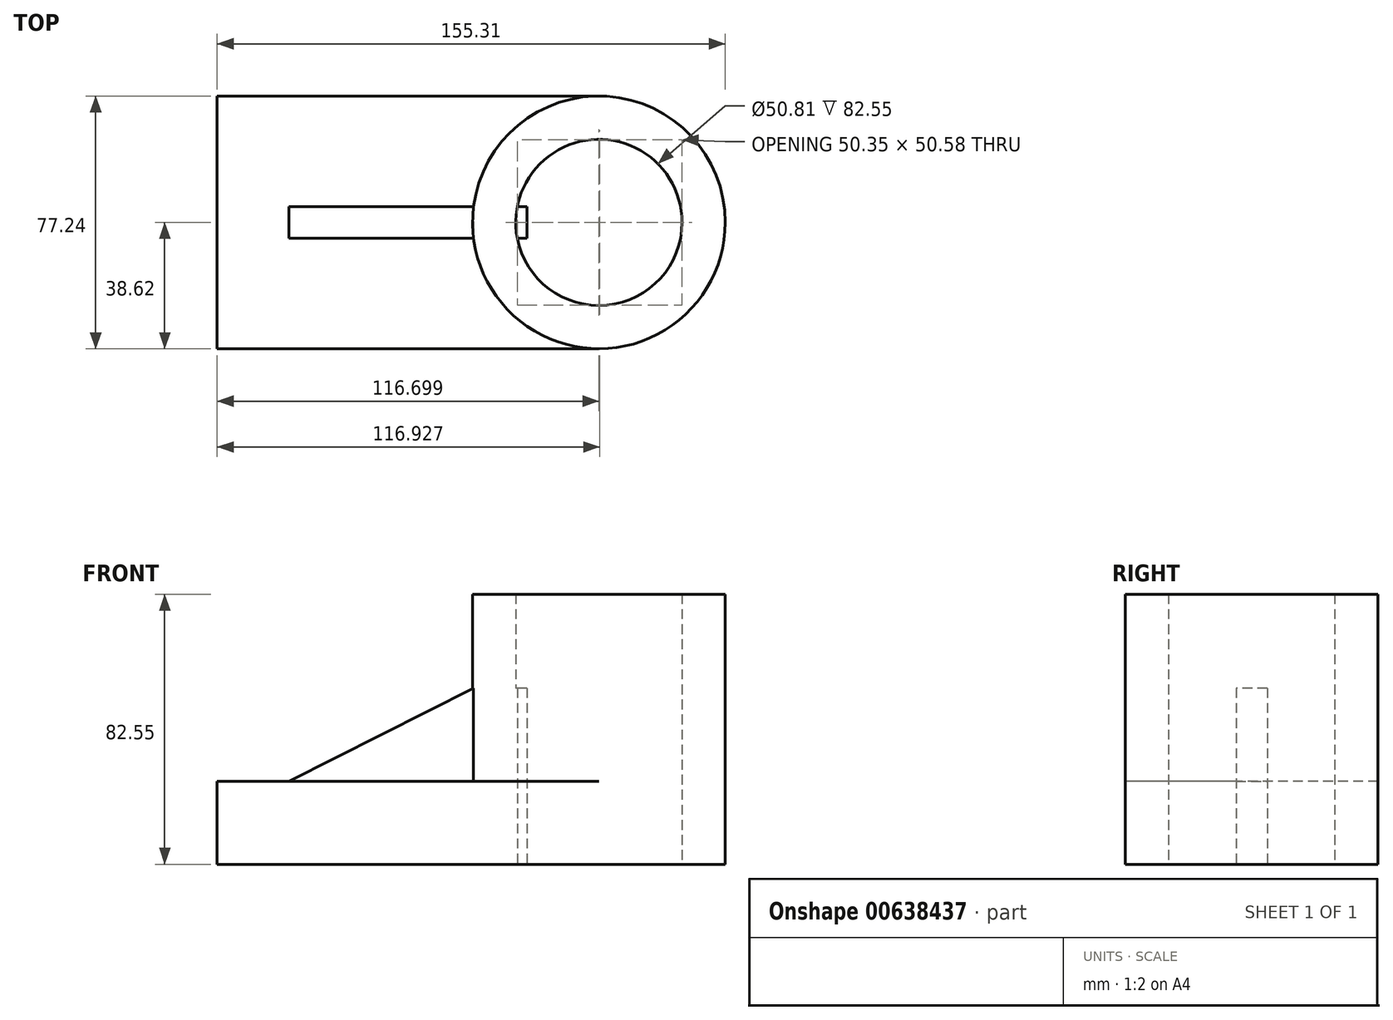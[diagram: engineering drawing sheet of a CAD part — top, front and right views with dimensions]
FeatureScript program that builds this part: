
annotation { "Feature Type Name" : "Feature", "Feature Type Description" : "" }
export const myFeature = defineFeature(function(context is Context, id is Id, definition is map)
    precondition{}
    {
        {
            var Q0;
            Q0=qCreatedBy(makeId("Top.planeOp"),FACE);
            var sketch = newSketch(context, id + "F0", { "sketchPlane" : qUnion([Q0])});
            skLineSegment(sketch, "E0.bottom", {"start": v(-58.35, 38.62) * mm, "end": v(58.35, 38.62) * mm});
            skLineSegment(sketch, "E0.top", {"start": v(-58.35, -38.62) * mm, "end": v(58.35, -38.62) * mm});
            skLineSegment(sketch, "E0.left", {"start": v(-58.35, 38.62) * mm, "end": v(-58.35, -38.62) * mm});
            skPoint(sketch, "E0.middle", {"position": v(0, 0) * mm});
            skCircle(sketch, "E1", {"center": v(58.35, 0) * mm, "radius": 38.62 * mm});
            skCircle(sketch, "E2", {"center": v(58.35, 0) * mm, "radius": 25.4 * mm});
            skSolve(sketch);
        }
        {
            var Q0;
            Q0=makeQuery(id+"F0.imprint","IMPRINT",FACE,{"disambiguationData":[TD([[makeQuery(id+"F0.imprint","IMPRINT",EDGE,{"derivedFrom":sQuery(id+"F0.wireOp",EDGE,"E2")}),-1.0]])]});
            extrude(context, id + "F1", {"entities" : qUnion([Q0]), "depth" : 82.55 * mm, "offsetDistance" : 25.4 * mm});
        }
        {
            var Q0;
            {var subQ0=sQuery(id+"F0.wireOp",EDGE,"E0.bottom");Q0=makeQuery(id+"F0.imprint","IMPRINT",FACE,{"disambiguationData":[TD([[makeQuery(id+"F0.imprint","IMPRINT",EDGE,{"derivedFrom":subQ0}),-1.0]])]});}
            extrude(context, id + "F2", {"entities" : qUnion([Q0]), "operationType" : NewBodyOperationType.ADD, "depth" : 25.4 * mm, "offsetDistance" : 25.4 * mm});
        }
        {
            var Q0;
            Q0=qCreatedBy(makeId("Top.planeOp"),FACE);
            var sketch = newSketch(context, id + "F3", { "sketchPlane" : qUnion([Q0])});
            skLineSegment(sketch, "E3.bottom", {"start": v(36.4, 4.8) * mm, "end": v(-36.4, 4.8) * mm});
            skLineSegment(sketch, "E3.top", {"start": v(36.4, -4.8) * mm, "end": v(-36.4, -4.8) * mm});
            skLineSegment(sketch, "E3.left", {"start": v(36.4, 4.8) * mm, "end": v(36.4, -4.8) * mm});
            skLineSegment(sketch, "E3.right", {"start": v(-36.4, 4.8) * mm, "end": v(-36.4, -4.8) * mm});
            skPoint(sketch, "E3.middle", {"position": v(0, 0) * mm});
            skSolve(sketch);
        }
        {
            var Q0;
            Q0 = qSketchRegion(id + "F3", true);
            extrude(context, id + "F4", {"entities" : qUnion([Q0]), "operationType" : NewBodyOperationType.ADD, "depth" : 53.85 * mm, "offsetDistance" : 25.4 * mm});
        }
        {
            var Q0;
            {var subQ2=sQuery(id+"F3.wireOp",EDGE,"E3.top");var subQ4=sQuery(id+"F0.wireOp",EDGE,"E1");Q0=makeQuery(id+"F4.boolean.opBoolean","SPLIT",FACE,{"disambiguationData":[TD([makeQuery(id+"F1.opExtrude","SWEPT_FACE",FACE,{"disambiguationData":[OSD([subQ4])]})])],"derivedFrom":makeQuery(id+"F4.opExtrude","SWEPT_FACE",FACE,{"disambiguationData":[OSD([subQ2])]})});}
            var sketch = newSketch(context, id + "F5", { "sketchPlane" : qUnion([Q0])});
            skLineSegment(sketch, "E4", {"start": v(20.03, 53.85) * mm, "end": v(-36.4, 25.4) * mm});
            skLineSegment(sketch, "E5", {"start": v(-36.4, 25.4) * mm, "end": v(20.03, 25.4) * mm});
            skLineSegment(sketch, "E6", {"start": v(20.03, 25.4) * mm, "end": v(20.03, 53.85) * mm});
            skSolve(sketch);
        }
        {
            var Q0;
            Q0=makeQuery(id+"F5.imprint","IMPRINT",FACE,{"disambiguationData":[TD([[makeQuery(id+"F5.imprint","IMPRINT",EDGE,{"derivedFrom":sQuery(id+"F5.wireOp",EDGE,"E4")}),-1.0]])]});
            extrude(context, id + "F6", {"entities" : qUnion([Q0]), "operationType" : NewBodyOperationType.REMOVE, "oppositeDirection" : true, "depth" : 25.4 * mm, "offsetDistance" : 25.4 * mm});
        }
    });
